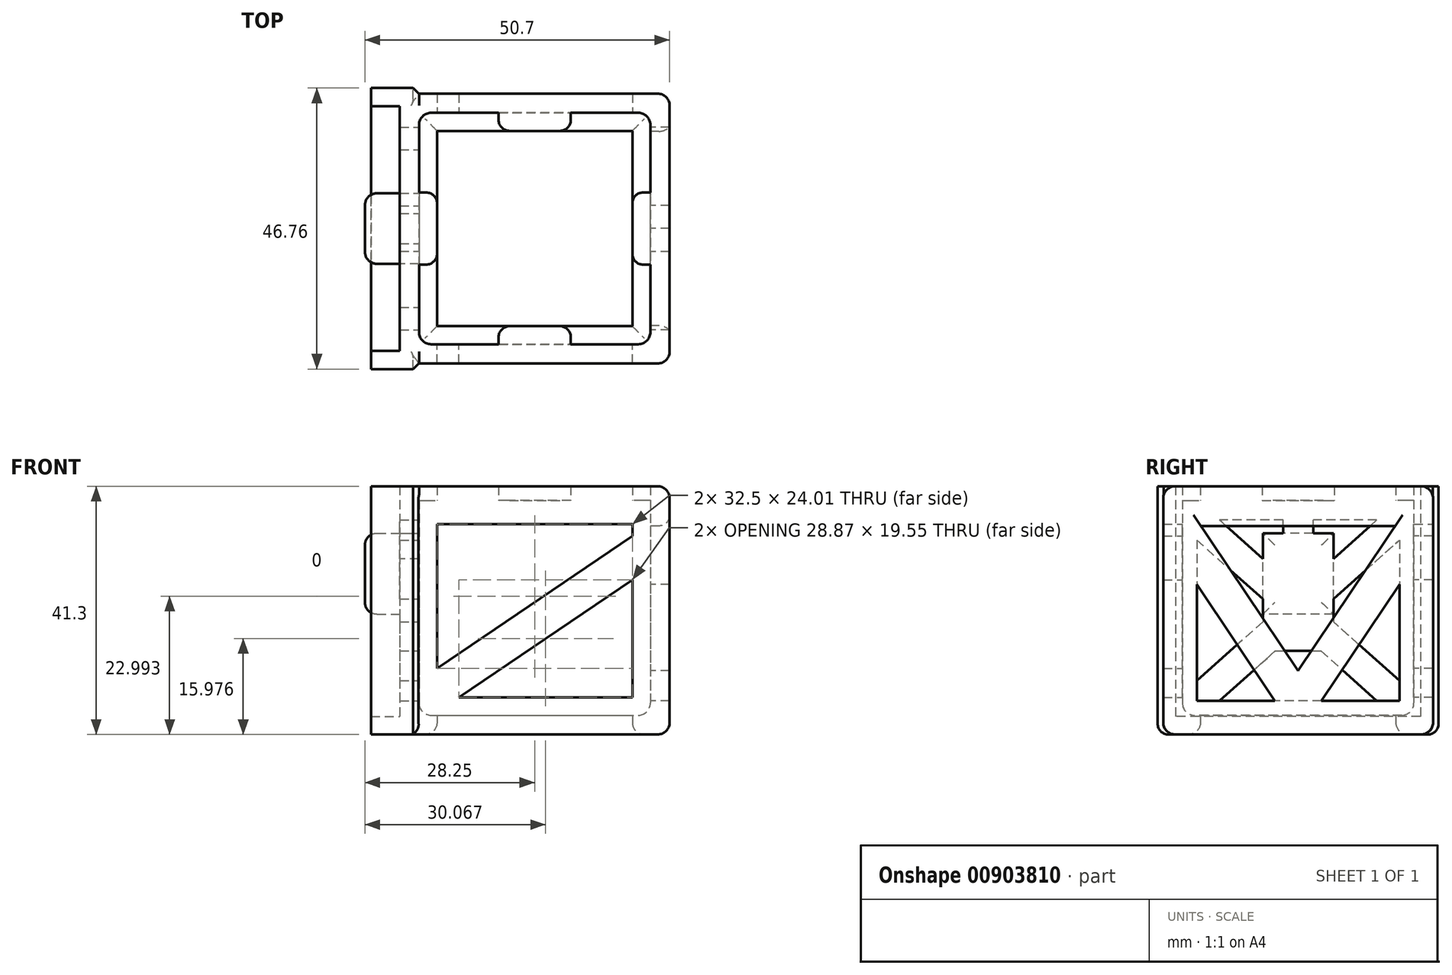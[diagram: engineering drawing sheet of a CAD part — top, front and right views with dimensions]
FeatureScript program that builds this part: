
annotation { "Feature Type Name" : "Feature", "Feature Type Description" : "" }
export const myFeature = defineFeature(function(context is Context, id is Id, definition is map)
    precondition{}
    {
        {
            var Q0;
            Q0=qCreatedBy(makeId("Top.planeOp"),FACE);
            var sketch = newSketch(context, id + "F0", { "sketchPlane" : qUnion([Q0])});
            skLineSegment(sketch, "E0.bottom", {"start": v(-22.45, 22.45) * mm, "end": v(22.45, 22.45) * mm});
            skLineSegment(sketch, "E0.top", {"start": v(-22.45, -22.45) * mm, "end": v(22.45, -22.45) * mm});
            skLineSegment(sketch, "E0.left", {"start": v(-22.45, 22.45) * mm, "end": v(-22.45, -22.45) * mm});
            skLineSegment(sketch, "E0.right", {"start": v(22.45, 22.45) * mm, "end": v(22.45, -22.45) * mm});
            skLineSegment(sketch, "E1.bottom", {"start": v(-19.25, 19.25) * mm, "end": v(19.25, 19.25) * mm});
            skLineSegment(sketch, "E1.top", {"start": v(-19.25, -19.25) * mm, "end": v(19.25, -19.25) * mm});
            skLineSegment(sketch, "E1.left", {"start": v(-19.25, 19.25) * mm, "end": v(-19.25, -19.25) * mm});
            skLineSegment(sketch, "E1.right", {"start": v(19.25, 19.25) * mm, "end": v(19.25, -19.25) * mm});
            skSolve(sketch);
        }
        {
            var Q0;
            Q0 = qSketchRegion(id + "F0", true);
            extrude(context, id + "F1", {"entities" : qUnion([Q0]), "depth" : 41.3 * mm, "offsetDistance" : 25 * mm});
        }
        {
            var Q0;
            Q0=makeQuery(id+"F1.opExtrude","CAP_FACE",FACE,{"disambiguationData":[OSD([sQuery(id+"F0.wireOp",EDGE,"E0.bottom"),sQuery(id+"F0.wireOp",EDGE,"E0.top"),sQuery(id+"F0.wireOp",EDGE,"E0.left"),sQuery(id+"F0.wireOp",EDGE,"E0.right"),sQuery(id+"F0.wireOp",EDGE,"E1.bottom"),sQuery(id+"F0.wireOp",EDGE,"E1.top"),sQuery(id+"F0.wireOp",EDGE,"E1.left"),sQuery(id+"F0.wireOp",EDGE,"E1.right")])],"isStart":false});
            cPlane(context, id + "F2", {"entities" : qUnion([Q0]), "cplaneType" : CPlaneType.OFFSET, "offset" : 2.35 * mm, "oppositeDirection" : true, "width" : 150 * mm, "height" : 150 * mm});
        }
        {
            var Q0;
            Q0=qCreatedBy(id+"F2.planeOp",FACE);
            var sketch = newSketch(context, id + "F3", { "sketchPlane" : qUnion([Q0])});
            skLineSegment(sketch, "E2.bottom", {"start": v(-19.25, 6) * mm, "end": v(-16.25, 6) * mm});
            skLineSegment(sketch, "E2.top", {"start": v(-19.25, -6) * mm, "end": v(-16.25, -6) * mm});
            skLineSegment(sketch, "E2.left", {"start": v(-19.25, 6) * mm, "end": v(-19.25, -6) * mm});
            skLineSegment(sketch, "E2.right", {"start": v(-16.25, 6) * mm, "end": v(-16.25, -6) * mm});
            skLineSegment(sketch, "E3.1.0", {"start": v(-6, -19.25) * mm, "end": v(6, -19.25) * mm});
            skLineSegment(sketch, "E3.1.1", {"start": v(6, -19.25) * mm, "end": v(6, -16.25) * mm});
            skLineSegment(sketch, "E3.1.2", {"start": v(-6, -16.25) * mm, "end": v(6, -16.25) * mm});
            skLineSegment(sketch, "E3.1.3", {"start": v(-6, -19.25) * mm, "end": v(-6, -16.25) * mm});
            skLineSegment(sketch, "E3.2.0", {"start": v(19.25, -6) * mm, "end": v(19.25, 6) * mm});
            skLineSegment(sketch, "E3.2.1", {"start": v(19.25, 6) * mm, "end": v(16.25, 6) * mm});
            skLineSegment(sketch, "E3.2.2", {"start": v(16.25, -6) * mm, "end": v(16.25, 6) * mm});
            skLineSegment(sketch, "E3.2.3", {"start": v(19.25, -6) * mm, "end": v(16.25, -6) * mm});
            skLineSegment(sketch, "E3.3.0", {"start": v(6, 19.25) * mm, "end": v(-6, 19.25) * mm});
            skLineSegment(sketch, "E3.3.1", {"start": v(-6, 19.25) * mm, "end": v(-6, 16.25) * mm});
            skLineSegment(sketch, "E3.3.2", {"start": v(6, 16.25) * mm, "end": v(-6, 16.25) * mm});
            skLineSegment(sketch, "E3.3.3", {"start": v(6, 19.25) * mm, "end": v(6, 16.25) * mm});
            skPoint(sketch, "E3.center", {"position": v(0, 0) * mm});
            skSolve(sketch);
        }
        {
            var Q0;
            Q0 = qSketchRegion(id + "F3", true);
            extrude(context, id + "F4", {"entities" : qUnion([Q0]), "operationType" : NewBodyOperationType.ADD, "depth" : 2.35 * mm, "offsetDistance" : 25 * mm});
        }
        {
            var Q0;
            Q0=qCreatedBy(makeId("Top.planeOp"),FACE);
            var sketch = newSketch(context, id + "F5", { "sketchPlane" : qUnion([Q0])});
            skLineSegment(sketch, "E4.bottom", {"start": v(-16.25, -16.25) * mm, "end": v(16.25, -16.25) * mm});
            skLineSegment(sketch, "E4.top", {"start": v(-16.25, 16.25) * mm, "end": v(16.25, 16.25) * mm});
            skLineSegment(sketch, "E4.left", {"start": v(-16.25, -16.25) * mm, "end": v(-16.25, 16.25) * mm});
            skLineSegment(sketch, "E4.right", {"start": v(16.25, -16.25) * mm, "end": v(16.25, 16.25) * mm});
            skLineSegment(sketch, "E5.bottom", {"start": v(22.45, 22.45) * mm, "end": v(-22.45, 22.45) * mm});
            skLineSegment(sketch, "E5.top", {"start": v(22.45, -22.45) * mm, "end": v(-22.45, -22.45) * mm});
            skLineSegment(sketch, "E5.left", {"start": v(22.45, 22.45) * mm, "end": v(22.45, -22.45) * mm});
            skLineSegment(sketch, "E5.right", {"start": v(-22.45, 22.45) * mm, "end": v(-22.45, -22.45) * mm});
            skSolve(sketch);
        }
        {
            var Q0;
            Q0 = qSketchRegion(id + "F5", true);
            extrude(context, id + "F6", {"entities" : qUnion([Q0]), "operationType" : NewBodyOperationType.ADD, "depth" : 3.2 * mm, "offsetDistance" : 25 * mm});
        }
        {
            var Q0;
            Q0=makeQuery(id+"F1.opExtrude","SWEPT_FACE",FACE,{"disambiguationData":[OSD([sQuery(id+"F0.wireOp",EDGE,"E1.top")])]});
            var sketch = newSketch(context, id + "F7", { "sketchPlane" : qUnion([Q0])});
            skLineSegment(sketch, "E6.bottom", {"start": v(-16.25, 35) * mm, "end": v(16.25, 35) * mm});
            skLineSegment(sketch, "E6.top", {"start": v(-16.25, 6.2) * mm, "end": v(16.25, 6.2) * mm});
            skLineSegment(sketch, "E6.left", {"start": v(16.25, 6.2) * mm, "end": v(16.25, 35) * mm});
            skLineSegment(sketch, "E6.right", {"start": v(-16.25, 6.2) * mm, "end": v(-16.25, 35) * mm});
            skSolve(sketch);
        }
        {
            var Q0;
            Q0=makeQuery(id+"F7.imprint","IMPRINT",FACE,{"disambiguationData":[TD([[makeQuery(id+"F7.imprint","IMPRINT",EDGE,{"derivedFrom":sQuery(id+"F7.wireOp",EDGE,"E6.bottom")}),-1.0]])]});
            extrude(context, id + "F8", {"entities" : qUnion([Q0]), "operationType" : NewBodyOperationType.REMOVE, "endBound" : BoundingType.SYMMETRIC, "oppositeDirection" : true, "depth" : 100 * mm, "offsetDistance" : 25 * mm});
        }
        {
            var Q0;
            Q0=makeQuery(id+"F1.opExtrude","SWEPT_FACE",FACE,{"disambiguationData":[OSD([sQuery(id+"F0.wireOp",EDGE,"E1.left")])]});
            var sketch = newSketch(context, id + "F9", { "sketchPlane" : qUnion([Q0])});
            skLineSegment(sketch, "E7.bottom", {"start": v(-16.85, 35.7) * mm, "end": v(16.85, 35.7) * mm});
            skLineSegment(sketch, "E7.top", {"start": v(-16.85, 5.6) * mm, "end": v(16.85, 5.6) * mm});
            skLineSegment(sketch, "E7.left", {"start": v(16.85, 5.6) * mm, "end": v(16.85, 35.7) * mm});
            skLineSegment(sketch, "E7.right", {"start": v(-16.85, 5.6) * mm, "end": v(-16.85, 35.7) * mm});
            skSolve(sketch);
        }
        {
            var Q0;
            Q0 = qSketchRegion(id + "F9", true);
            extrude(context, id + "F10", {"entities" : qUnion([Q0]), "operationType" : NewBodyOperationType.REMOVE, "endBound" : BoundingType.SYMMETRIC, "depth" : 100 * mm, "offsetDistance" : 25 * mm});
        }
        {
            var Q0;
            Q0=makeQuery(id+"F1.opExtrude","SWEPT_FACE",FACE,{"disambiguationData":[OSD([sQuery(id+"F0.wireOp",EDGE,"E1.left")])]});
            var sketch = newSketch(context, id + "F11", { "sketchPlane" : qUnion([Q0])});
            skLineSegment(sketch, "E8", {"start": v(16.85, 8.95) * mm, "end": v(5.88, 18.75) * mm});
            skLineSegment(sketch, "E9", {"start": v(-16.85, 32.35) * mm, "end": v(-5.88, 22.55) * mm});
            skLineSegment(sketch, "E10", {"start": v(13.1, 35.7) * mm, "end": v(3.8, 27.4) * mm});
            skLineSegment(sketch, "E11", {"start": v(-13.1, 5.6) * mm, "end": v(-3.8, 13.9) * mm});
            skLineSegment(sketch, "E12.trimOffspring", {"start": v(-5.88, 18.75) * mm, "end": v(-16.85, 8.95) * mm});
            skLineSegment(sketch, "E13.trimOffspring", {"start": v(3.8, 13.9) * mm, "end": v(13.1, 5.6) * mm});
            skLineSegment(sketch, "E14.trimOffspring", {"start": v(5.88, 22.55) * mm, "end": v(16.85, 32.35) * mm});
            skLineSegment(sketch, "E15.trimOffspring", {"start": v(-3.8, 27.4) * mm, "end": v(-13.1, 35.7) * mm});
            skLineSegment(sketch, "E16", {"start": v(-16.85, 5.6) * mm, "end": v(16.85, 35.7) * mm, "construction": true});
            skLineSegment(sketch, "E17", {"start": v(-16.85, 35.7) * mm, "end": v(16.85, 5.6) * mm, "construction": true});
            skLineSegment(sketch, "E18.bottom", {"start": v(-3.8, 27.4) * mm, "end": v(-2.5, 27.4) * mm});
            skLineSegment(sketch, "E18.top", {"start": v(-3.8, 13.9) * mm, "end": v(3.8, 13.9) * mm});
            skLineSegment(sketch, "E19.trimOffspring", {"start": v(-5.88, 22.55) * mm, "end": v(-5.88, 18.75) * mm});
            skLineSegment(sketch, "E20.trimOffspring", {"start": v(5.87, 22.55) * mm, "end": v(5.88, 18.75) * mm});
            skLineSegment(sketch, "E21.bottom", {"start": v(-13.1, 35.7) * mm, "end": v(13.1, 35.7) * mm});
            skLineSegment(sketch, "E21.top", {"start": v(-13.1, 5.6) * mm, "end": v(13.1, 5.6) * mm});
            skLineSegment(sketch, "E21.right", {"start": v(16.85, 32.35) * mm, "end": v(16.85, 8.95) * mm});
            skLineSegment(sketch, "E22.trimOffspring", {"start": v(-16.85, 32.35) * mm, "end": v(-16.85, 8.95) * mm});
            skPoint(sketch, "E23", {"position": v(0, 20.65) * mm});
            skLineSegment(sketch, "E24", {"start": v(2.5, 27.4) * mm, "end": v(2.5, 35.7) * mm});
            skLineSegment(sketch, "E25", {"start": v(-2.5, 27.4) * mm, "end": v(-2.5, 35.7) * mm});
            skLineSegment(sketch, "E26.trimOffspring", {"start": v(2.5, 27.4) * mm, "end": v(3.8, 27.4) * mm});
            skSolve(sketch);
        }
        {
            var Q0;
            {var subQ4=sQuery(id+"F11.wireOp",EDGE,"E8");Q0=makeQuery(id+"F11.imprint","IMPRINT",FACE,{"disambiguationData":[TD([[makeQuery(id+"F11.imprint","IMPRINT",EDGE,{"derivedFrom":subQ4}),1.0]])]});}
            extrude(context, id + "F12", {"entities" : qUnion([Q0]), "operationType" : NewBodyOperationType.ADD, "oppositeDirection" : true, "depth" : 3.2 * mm, "offsetDistance" : 25 * mm});
        }
        {
            var Q0;
            Q0=makeQuery(id+"F11.imprint","IMPRINT",FACE,{"disambiguationData":[TD([[makeQuery(id+"F11.imprint","IMPRINT",EDGE,{"derivedFrom":sQuery(id+"F11.wireOp",EDGE,"E9")}),-1.0]])]});
            var sketch = newSketch(context, id + "F13", { "sketchPlane" : qUnion([Q0])});
            skLineSegment(sketch, "E27", {"start": v(-23.38, 0) * mm, "end": v(-23.38, 41.3) * mm});
            skLineSegment(sketch, "E28", {"start": v(-23.38, 41.3) * mm, "end": v(-20.38, 41.3) * mm});
            skLineSegment(sketch, "E29", {"start": v(23.37, 41.3) * mm, "end": v(23.38, 0) * mm});
            skLineSegment(sketch, "E30", {"start": v(-23.38, 0) * mm, "end": v(23.37, 0) * mm});
            skLineSegment(sketch, "E31.left", {"start": v(-20.38, 41.3) * mm, "end": v(-20.38, 3) * mm});
            skLineSegment(sketch, "E31.right", {"start": v(20.37, 41.3) * mm, "end": v(20.38, 3) * mm});
            skLineSegment(sketch, "E32.trimOffspring", {"start": v(20.37, 41.3) * mm, "end": v(23.37, 41.3) * mm});
            skLineSegment(sketch, "E33", {"start": v(20.38, 3) * mm, "end": v(-20.38, 3) * mm});
            skSolve(sketch);
        }
        {
            var Q0;
            Q0 = qSketchRegion(id + "F13", true);
            extrude(context, id + "F14", {"entities" : qUnion([Q0]), "operationType" : NewBodyOperationType.ADD, "oppositeDirection" : true, "depth" : 8 * mm, "offsetDistance" : 25 * mm, "hasSecondDirection" : true, "secondDirectionOppositeDirection" : false, "secondDirectionDepth" : 0 * mm});
        }
        {
            var Q0;
            Q0=makeQuery(id+"F1.opExtrude","SWEPT_FACE",FACE,{"disambiguationData":[OSD([sQuery(id+"F0.wireOp",EDGE,"E1.right")])]});
            var sketch = newSketch(context, id + "F15", { "sketchPlane" : qUnion([Q0])});
            skLineSegment(sketch, "E34", {"start": v(-3.87, 5.6) * mm, "end": v(-16.85, 24.94) * mm});
            skLineSegment(sketch, "E35", {"start": v(16.18, 34.7) * mm, "end": v(0, 10.6) * mm});
            skLineSegment(sketch, "E36", {"start": v(16.85, 24.94) * mm, "end": v(3.87, 5.6) * mm});
            skLineSegment(sketch, "E37", {"start": v(0, 10.6) * mm, "end": v(-16.18, 34.7) * mm});
            skLineSegment(sketch, "E38", {"start": v(16.85, 24.94) * mm, "end": v(16.85, 35.7) * mm});
            skLineSegment(sketch, "E39", {"start": v(16.18, 34.7) * mm, "end": v(-16.18, 34.7) * mm});
            skSolve(sketch);
        }
        {
            var Q0;
            Q0=makeQuery(id+"F15.imprint","IMPRINT",FACE,{"disambiguationData":[TD([[makeQuery(id+"F15.imprint","IMPRINT",EDGE,{"derivedFrom":sQuery(id+"F15.wireOp",EDGE,"E34")}),-1.0]])]});
            extrude(context, id + "F16", {"entities" : qUnion([Q0]), "operationType" : NewBodyOperationType.ADD, "oppositeDirection" : true, "depth" : 3.2 * mm, "offsetDistance" : 25 * mm});
        }
        {
            var Q0;
            {var subQ0=sQuery(id+"F11.wireOp",EDGE,"E8");var subQ1=sQuery(id+"F0.wireOp",EDGE,"E1.left");Q0=makeQuery(id+"F12.boolean.opBoolean","MERGE",FACE,{"derivedFrom":[makeQuery(id+"F1.opExtrude","SWEPT_FACE",FACE,{"disambiguationData":[OSD([subQ1])]}),makeQuery(id+"F12.opExtrude","CAP_FACE",FACE,{"disambiguationData":[OSD([sQuery(id+"F0.wireOp",EDGE,"E1.top"),subQ1,sQuery(id+"F11.wireOp",EDGE,"8725238e-58d9-4992-a780-614409748a7c.top"),sQuery(id+"F11.wireOp",EDGE,"8725238e-58d9-4992-a780-614409748a7c.right"),subQ0])],"isStart":true}),makeQuery(id+"F12.opExtrude","CAP_FACE",FACE,{"disambiguationData":[OSD([subQ1,sQuery(id+"F9.wireOp",EDGE,"E7.bottom"),sQuery(id+"F9.wireOp",EDGE,"E7.top"),sQuery(id+"F9.wireOp",EDGE,"E7.left"),sQuery(id+"F9.wireOp",EDGE,"E7.right"),subQ0,sQuery(id+"F11.wireOp",EDGE,"E9"),sQuery(id+"F11.wireOp",EDGE,"E10"),sQuery(id+"F11.wireOp",EDGE,"E11"),sQuery(id+"F11.wireOp",EDGE,"E12.trimOffspring"),sQuery(id+"F11.wireOp",EDGE,"E13.trimOffspring"),sQuery(id+"F11.wireOp",EDGE,"E14.trimOffspring"),sQuery(id+"F11.wireOp",EDGE,"E15.trimOffspring"),sQuery(id+"F11.wireOp",EDGE,"E18.bottom"),sQuery(id+"F11.wireOp",EDGE,"E18.top"),sQuery(id+"F11.wireOp",EDGE,"E19.trimOffspring"),sQuery(id+"F11.wireOp",EDGE,"E20.trimOffspring")])],"isStart":true})]});}
            var sketch = newSketch(context, id + "F17", { "sketchPlane" : qUnion([Q0])});
            skLineSegment(sketch, "E40.bottom", {"start": v(5.87, 20) * mm, "end": v(-5.88, 20) * mm});
            skLineSegment(sketch, "E40.top", {"start": v(5.87, 33.5) * mm, "end": v(-5.88, 33.5) * mm});
            skLineSegment(sketch, "E40.left", {"start": v(5.87, 20) * mm, "end": v(5.87, 33.5) * mm});
            skLineSegment(sketch, "E40.right", {"start": v(-5.88, 20) * mm, "end": v(-5.88, 33.5) * mm});
            skSolve(sketch);
        }
        {
            var Q0;
            Q0 = qSketchRegion(id + "F17", true);
            extrude(context, id + "F18", {"entities" : qUnion([Q0]), "operationType" : NewBodyOperationType.ADD, "oppositeDirection" : true, "depth" : 9 * mm, "offsetDistance" : 25 * mm});
        }
        {
            var Q0;
            Q0=makeQuery(id+"F1.opExtrude","SWEPT_FACE",FACE,{"disambiguationData":[OSD([sQuery(id+"F0.wireOp",EDGE,"E1.bottom")])]});
            var sketch = newSketch(context, id + "F19", { "sketchPlane" : qUnion([Q0])});
            skLineSegment(sketch, "E41", {"start": v(16.25, 25.75) * mm, "end": v(-12.62, 6.2) * mm});
            skLineSegment(sketch, "E42", {"start": v(-16.25, 10.99) * mm, "end": v(16.25, 33) * mm});
            skSolve(sketch);
        }
        {
            var Q0;
            {var subQ5=sQuery(id+"F19.wireOp",EDGE,"E41");Q0=makeQuery(id+"F19.imprint","IMPRINT",FACE,{"disambiguationData":[TD([[makeQuery(id+"F19.imprint","IMPRINT",EDGE,{"derivedFrom":subQ5}),-1.0]])]});}
            extrude(context, id + "F20", {"entities" : qUnion([Q0]), "operationType" : NewBodyOperationType.ADD, "oppositeDirection" : true, "depth" : 3.2 * mm, "offsetDistance" : 25 * mm});
        }
        {
            var Q0;
            Q0=makeQuery(id+"F1.opExtrude","SWEPT_FACE",FACE,{"disambiguationData":[OSD([sQuery(id+"F0.wireOp",EDGE,"E1.top")])]});
            var sketch = newSketch(context, id + "F21", { "sketchPlane" : qUnion([Q0])});
            skLineSegment(sketch, "E43.0", {"start": v(-16.25, 25.75) * mm, "end": v(12.62, 6.2) * mm});
            skLineSegment(sketch, "E43.1", {"start": v(16.25, 10.99) * mm, "end": v(-16.25, 33) * mm});
            skSolve(sketch);
        }
        {
            var Q0;
            Q0=makeQuery(id+"F1.opExtrude","CAP_EDGE",EDGE,{"disambiguationData":[OSD([sQuery(id+"F0.wireOp",EDGE,"E0.bottom")])],"isStart":true});
            var Q1;
            Q1=makeQuery(id+"F1.opExtrude","SWEPT_EDGE",EDGE,{"disambiguationData":[OSD([sQuery(id+"F0.wireOp",EDGE,"E0.bottom"),sQuery(id+"F0.wireOp",EDGE,"E0.right")])]});
            var Q2;
            Q2=makeQuery(id+"F1.opExtrude","CAP_EDGE",EDGE,{"disambiguationData":[OSD([sQuery(id+"F0.wireOp",EDGE,"E0.bottom")])],"isStart":false});
            var Q3;
            Q3=makeQuery(id+"F6.boolean.opBoolean","INTERSECT",EDGE,{"derivedFrom":[makeQuery(id+"F1.opExtrude","SWEPT_FACE",FACE,{"disambiguationData":[OSD([sQuery(id+"F0.wireOp",EDGE,"E1.bottom")])]}),makeQuery(id+"F6.opExtrude","CAP_FACE",FACE,{"disambiguationData":[OSD([sQuery(id+"F5.wireOp",EDGE,"E4.bottom"),sQuery(id+"F5.wireOp",EDGE,"E4.top"),sQuery(id+"F5.wireOp",EDGE,"E4.left"),sQuery(id+"F5.wireOp",EDGE,"E4.right"),sQuery(id+"F5.wireOp",EDGE,"E5.bottom"),sQuery(id+"F5.wireOp",EDGE,"E5.top"),sQuery(id+"F5.wireOp",EDGE,"E5.left"),sQuery(id+"F5.wireOp",EDGE,"E5.right")])],"isStart":false})]});
            var Q4;
            Q4=makeQuery(id+"F6.boolean.opBoolean","INTERSECT",EDGE,{"derivedFrom":[makeQuery(id+"F1.opExtrude","SWEPT_FACE",FACE,{"disambiguationData":[OSD([sQuery(id+"F0.wireOp",EDGE,"E1.top")])]}),makeQuery(id+"F6.opExtrude","CAP_FACE",FACE,{"disambiguationData":[OSD([sQuery(id+"F5.wireOp",EDGE,"E4.bottom"),sQuery(id+"F5.wireOp",EDGE,"E4.top"),sQuery(id+"F5.wireOp",EDGE,"E4.left"),sQuery(id+"F5.wireOp",EDGE,"E4.right"),sQuery(id+"F5.wireOp",EDGE,"E5.bottom"),sQuery(id+"F5.wireOp",EDGE,"E5.top"),sQuery(id+"F5.wireOp",EDGE,"E5.left"),sQuery(id+"F5.wireOp",EDGE,"E5.right")])],"isStart":false})]});
            var Q5;
            Q5=makeQuery(id+"F1.opExtrude","CAP_EDGE",EDGE,{"disambiguationData":[OSD([sQuery(id+"F0.wireOp",EDGE,"E0.top")])],"isStart":true});
            var Q6;
            Q6=makeQuery(id+"F1.opExtrude","CAP_EDGE",EDGE,{"disambiguationData":[OSD([sQuery(id+"F0.wireOp",EDGE,"E0.right")])],"isStart":true});
            var Q7;
            Q7=makeQuery(id+"F1.opExtrude","SWEPT_EDGE",EDGE,{"disambiguationData":[OSD([sQuery(id+"F0.wireOp",EDGE,"E0.top"),sQuery(id+"F0.wireOp",EDGE,"E0.right")])]});
            var Q8;
            Q8=makeQuery(id+"F6.opExtrude","CAP_EDGE",EDGE,{"disambiguationData":[OSD([sQuery(id+"F5.wireOp",EDGE,"E4.left")])],"isStart":true});
            var Q9;
            Q9=makeQuery(id+"F6.opExtrude","CAP_EDGE",EDGE,{"disambiguationData":[OSD([sQuery(id+"F5.wireOp",EDGE,"E4.bottom")])],"isStart":true});
            var Q10;
            Q10=makeQuery(id+"F6.opExtrude","CAP_EDGE",EDGE,{"disambiguationData":[OSD([sQuery(id+"F5.wireOp",EDGE,"E4.right")])],"isStart":true});
            var Q11;
            Q11=makeQuery(id+"F6.opExtrude","CAP_EDGE",EDGE,{"disambiguationData":[OSD([sQuery(id+"F5.wireOp",EDGE,"E4.top")])],"isStart":true});
            var Q12;
            Q12=makeQuery(id+"F1.opExtrude","CAP_EDGE",EDGE,{"disambiguationData":[OSD([sQuery(id+"F0.wireOp",EDGE,"E0.top")])],"isStart":false});
            var Q13;
            Q13=makeQuery(id+"F1.opExtrude","CAP_EDGE",EDGE,{"disambiguationData":[OSD([sQuery(id+"F0.wireOp",EDGE,"E0.right")])],"isStart":false});
            var Q14;
            Q14=makeQuery(id+"F4.opExtrude","SWEPT_EDGE",EDGE,{"disambiguationData":[OSD([sQuery(id+"F3.wireOp",EDGE,"E3.3.0"),sQuery(id+"F3.wireOp",EDGE,"E3.3.3")])]});
            var Q15;
            Q15=makeQuery(id+"F4.opExtrude","SWEPT_EDGE",EDGE,{"disambiguationData":[OSD([sQuery(id+"F3.wireOp",EDGE,"E3.3.0"),sQuery(id+"F3.wireOp",EDGE,"E3.3.1")])]});
            var Q16;
            Q16=makeQuery(id+"F4.opExtrude","SWEPT_EDGE",EDGE,{"disambiguationData":[OSD([sQuery(id+"F3.wireOp",EDGE,"E3.2.0"),sQuery(id+"F3.wireOp",EDGE,"E3.2.3")])]});
            var Q17;
            Q17=makeQuery(id+"F4.opExtrude","SWEPT_EDGE",EDGE,{"disambiguationData":[OSD([sQuery(id+"F3.wireOp",EDGE,"E3.2.0"),sQuery(id+"F3.wireOp",EDGE,"E3.2.1")])]});
            var Q18;
            Q18=makeQuery(id+"F4.opExtrude","SWEPT_EDGE",EDGE,{"disambiguationData":[OSD([sQuery(id+"F3.wireOp",EDGE,"E3.1.0"),sQuery(id+"F3.wireOp",EDGE,"E3.1.3")])]});
            var Q19;
            Q19=makeQuery(id+"F4.opExtrude","SWEPT_EDGE",EDGE,{"disambiguationData":[OSD([sQuery(id+"F3.wireOp",EDGE,"E3.1.0"),sQuery(id+"F3.wireOp",EDGE,"E3.1.1")])]});
            var Q20;
            Q20=makeQuery(id+"F4.opExtrude","SWEPT_EDGE",EDGE,{"disambiguationData":[OSD([sQuery(id+"F3.wireOp",EDGE,"E2.bottom"),sQuery(id+"F3.wireOp",EDGE,"E2.left")])]});
            var Q21;
            Q21=makeQuery(id+"F4.opExtrude","SWEPT_EDGE",EDGE,{"disambiguationData":[OSD([sQuery(id+"F3.wireOp",EDGE,"E2.top"),sQuery(id+"F3.wireOp",EDGE,"E2.left")])]});
            var Q22;
            Q22=makeQuery(id+"F1.opExtrude","SWEPT_EDGE",EDGE,{"disambiguationData":[OSD([sQuery(id+"F0.wireOp",EDGE,"E1.top"),sQuery(id+"F0.wireOp",EDGE,"E1.left")])]});
            var Q23;
            Q23=makeQuery(id+"F1.opExtrude","SWEPT_EDGE",EDGE,{"disambiguationData":[OSD([sQuery(id+"F0.wireOp",EDGE,"E1.bottom"),sQuery(id+"F0.wireOp",EDGE,"E1.left")])]});
            var Q24;
            Q24=makeQuery(id+"F6.boolean.opBoolean","INTERSECT",EDGE,{"derivedFrom":[makeQuery(id+"F1.opExtrude","SWEPT_FACE",FACE,{"disambiguationData":[OSD([sQuery(id+"F0.wireOp",EDGE,"E1.right")])]}),makeQuery(id+"F6.opExtrude","CAP_FACE",FACE,{"disambiguationData":[OSD([sQuery(id+"F5.wireOp",EDGE,"E4.bottom"),sQuery(id+"F5.wireOp",EDGE,"E4.top"),sQuery(id+"F5.wireOp",EDGE,"E4.left"),sQuery(id+"F5.wireOp",EDGE,"E4.right"),sQuery(id+"F5.wireOp",EDGE,"E5.bottom"),sQuery(id+"F5.wireOp",EDGE,"E5.top"),sQuery(id+"F5.wireOp",EDGE,"E5.left"),sQuery(id+"F5.wireOp",EDGE,"E5.right")])],"isStart":false})]});
            var Q25;
            Q25=makeQuery(id+"F1.opExtrude","SWEPT_EDGE",EDGE,{"disambiguationData":[OSD([sQuery(id+"F0.wireOp",EDGE,"E1.top"),sQuery(id+"F0.wireOp",EDGE,"E1.right")])]});
            var Q26;
            Q26=makeQuery(id+"F1.opExtrude","SWEPT_EDGE",EDGE,{"disambiguationData":[OSD([sQuery(id+"F0.wireOp",EDGE,"E1.bottom"),sQuery(id+"F0.wireOp",EDGE,"E1.right")])]});
            var Q27;
            Q27=makeQuery(id+"F18.opExtrude","CAP_EDGE",EDGE,{"disambiguationData":[OSD([sQuery(id+"F17.wireOp",EDGE,"E40.top")])],"isStart":false});
            var Q28;
            Q28=makeQuery(id+"F18.opExtrude","CAP_EDGE",EDGE,{"disambiguationData":[OSD([sQuery(id+"F17.wireOp",EDGE,"E40.right")])],"isStart":false});
            var Q29;
            Q29=makeQuery(id+"F18.opExtrude","CAP_EDGE",EDGE,{"disambiguationData":[OSD([sQuery(id+"F17.wireOp",EDGE,"E40.bottom")])],"isStart":false});
            var Q30;
            Q30=makeQuery(id+"F18.opExtrude","CAP_EDGE",EDGE,{"disambiguationData":[OSD([sQuery(id+"F17.wireOp",EDGE,"E40.left")])],"isStart":false});
            var Q31;
            Q31=makeQuery(id+"F6.boolean.opBoolean","INTERSECT",EDGE,{"derivedFrom":[makeQuery(id+"F1.opExtrude","SWEPT_FACE",FACE,{"disambiguationData":[OSD([sQuery(id+"F0.wireOp",EDGE,"E1.left")])]}),makeQuery(id+"F6.opExtrude","CAP_FACE",FACE,{"disambiguationData":[OSD([sQuery(id+"F5.wireOp",EDGE,"E4.bottom"),sQuery(id+"F5.wireOp",EDGE,"E4.top"),sQuery(id+"F5.wireOp",EDGE,"E4.left"),sQuery(id+"F5.wireOp",EDGE,"E4.right"),sQuery(id+"F5.wireOp",EDGE,"E5.bottom"),sQuery(id+"F5.wireOp",EDGE,"E5.top"),sQuery(id+"F5.wireOp",EDGE,"E5.left"),sQuery(id+"F5.wireOp",EDGE,"E5.right")])],"isStart":false})]});
            fillet(context, id + "F22", {"entities" : qUnion([Q0, Q1, Q2, Q3, Q4, Q5, Q6, Q7, Q8, Q9, Q10, Q11, Q12, Q13, Q14, Q15, Q16, Q17, Q18, Q19, Q20, Q21, Q22, Q23, Q24, Q25, Q26, Q27, Q28, Q29, Q30, Q31]), "radius" : 2 * mm, "allowEdgeOverflow" : false});
        }
        {
            var Q0;
            Q0=makeQuery(id+"F4.opExtrude","SWEPT_EDGE",EDGE,{"disambiguationData":[OSD([sQuery(id+"F3.wireOp",EDGE,"E2.bottom"),sQuery(id+"F3.wireOp",EDGE,"E2.right")])]});
            var Q1;
            Q1=makeQuery(id+"F4.opExtrude","SWEPT_EDGE",EDGE,{"disambiguationData":[OSD([sQuery(id+"F3.wireOp",EDGE,"E2.top"),sQuery(id+"F3.wireOp",EDGE,"E2.right")])]});
            var Q2;
            Q2=makeQuery(id+"F4.opExtrude","SWEPT_EDGE",EDGE,{"disambiguationData":[OSD([sQuery(id+"F3.wireOp",EDGE,"E3.1.2"),sQuery(id+"F3.wireOp",EDGE,"E3.1.3")])]});
            var Q3;
            Q3=makeQuery(id+"F4.opExtrude","SWEPT_EDGE",EDGE,{"disambiguationData":[OSD([sQuery(id+"F3.wireOp",EDGE,"E3.1.1"),sQuery(id+"F3.wireOp",EDGE,"E3.1.2")])]});
            var Q4;
            Q4=makeQuery(id+"F4.opExtrude","SWEPT_EDGE",EDGE,{"disambiguationData":[OSD([sQuery(id+"F3.wireOp",EDGE,"E3.3.2"),sQuery(id+"F3.wireOp",EDGE,"E3.3.3")])]});
            var Q5;
            Q5=makeQuery(id+"F4.opExtrude","SWEPT_EDGE",EDGE,{"disambiguationData":[OSD([sQuery(id+"F3.wireOp",EDGE,"E3.2.2"),sQuery(id+"F3.wireOp",EDGE,"E3.2.3")])]});
            var Q6;
            Q6=makeQuery(id+"F4.opExtrude","SWEPT_EDGE",EDGE,{"disambiguationData":[OSD([sQuery(id+"F3.wireOp",EDGE,"E3.2.1"),sQuery(id+"F3.wireOp",EDGE,"E3.2.2")])]});
            var Q7;
            Q7=makeQuery(id+"F4.opExtrude","SWEPT_EDGE",EDGE,{"disambiguationData":[OSD([sQuery(id+"F3.wireOp",EDGE,"E3.3.1"),sQuery(id+"F3.wireOp",EDGE,"E3.3.2")])]});
            var Q8;
            Q8=makeQuery(id+"F14.opExtrude","SWEPT_EDGE",EDGE,{"disambiguationData":[OSD([sQuery(id+"F13.wireOp",EDGE,"E27"),sQuery(id+"F13.wireOp",EDGE,"E30")])]});
            var Q9;
            Q9=makeQuery(id+"F14.opExtrude","SWEPT_EDGE",EDGE,{"disambiguationData":[OSD([sQuery(id+"F13.wireOp",EDGE,"E29"),sQuery(id+"F13.wireOp",EDGE,"E30")])]});
            var Q10;
            Q10=makeQuery(id+"F16.opExtrude","CAP_EDGE",EDGE,{"disambiguationData":[OSD([sQuery(id+"F15.wireOp",EDGE,"E39")])],"isStart":false});
            fillet(context, id + "F23", {"entities" : qUnion([Q0, Q1, Q2, Q3, Q4, Q5, Q6, Q7, Q8, Q9, Q10]), "radius" : 1.8 * mm, "tangentPropagation" : true, "allowEdgeOverflow" : false});
        }
        {
            var Q0;
            Q0=makeQuery(id+"F14.opExtrude","CAP_EDGE",EDGE,{"disambiguationData":[OSD([sQuery(id+"F13.wireOp",EDGE,"E27")])],"isStart":true});
            var Q1;
            {var subQ0=sQuery(id+"F13.wireOp",EDGE,"E28");var subQ1=sQuery(id+"F13.wireOp",EDGE,"E27");var subQ8=sQuery(id+"F0.wireOp",EDGE,"E0.top");var subQ10=sQuery(id+"F13.wireOp",EDGE,"E32.trimOffspring");var subQ11=sQuery(id+"F13.wireOp",EDGE,"E30");Q1=makeQuery(id+"F23.opFillet","BLEND_EDGE",EDGE,{"blendedFrom":[makeQuery(id+"F14.opExtrude","SWEPT_EDGE",EDGE,{"disambiguationData":[OSD([subQ1,subQ0])]}),makeQuery(id+"F14.boolean.opBoolean","SPLIT",FACE,{"disambiguationData":[TD([makeQuery(id+"F1.opExtrude","SWEPT_FACE",FACE,{"disambiguationData":[OSD([subQ8])]})])],"derivedFrom":makeQuery(id+"F14.opExtrude","CAP_FACE",FACE,{"disambiguationData":[OSD([subQ1,subQ0,sQuery(id+"F13.wireOp",EDGE,"E29"),subQ11,sQuery(id+"F13.wireOp",EDGE,"E31.left"),sQuery(id+"F13.wireOp",EDGE,"E31.right"),subQ10,sQuery(id+"F13.wireOp",EDGE,"E33")])],"isStart":true})})],"blendedInto":[makeQuery(id+"F14.boolean.opBoolean","SPLIT",FACE,{"disambiguationData":[TD([makeQuery(id+"F1.opExtrude","SWEPT_FACE",FACE,{"disambiguationData":[OSD([subQ8])]})])],"derivedFrom":makeQuery(id+"F14.opExtrude","CAP_FACE",FACE,{"disambiguationData":[OSD([subQ1,subQ0,sQuery(id+"F13.wireOp",EDGE,"E29"),subQ11,sQuery(id+"F13.wireOp",EDGE,"E31.left"),sQuery(id+"F13.wireOp",EDGE,"E31.right"),subQ10,sQuery(id+"F13.wireOp",EDGE,"E33")])],"isStart":true})})]});}
            var Q2;
            {var subQ0=sQuery(id+"F13.wireOp",EDGE,"E28");var subQ1=sQuery(id+"F13.wireOp",EDGE,"E27");var subQ8=sQuery(id+"F0.wireOp",EDGE,"E0.top");var subQ10=sQuery(id+"F13.wireOp",EDGE,"E32.trimOffspring");var subQ11=sQuery(id+"F13.wireOp",EDGE,"E30");Q2=makeQuery(id+"F23.opFillet","BLEND_EDGE",EDGE,{"blendedFrom":[makeQuery(id+"F14.opExtrude","SWEPT_EDGE",EDGE,{"disambiguationData":[OSD([subQ1,subQ11])]}),makeQuery(id+"F14.boolean.opBoolean","SPLIT",FACE,{"disambiguationData":[TD([makeQuery(id+"F1.opExtrude","SWEPT_FACE",FACE,{"disambiguationData":[OSD([subQ8])]})])],"derivedFrom":makeQuery(id+"F14.opExtrude","CAP_FACE",FACE,{"disambiguationData":[OSD([subQ1,subQ0,sQuery(id+"F13.wireOp",EDGE,"E29"),subQ11,sQuery(id+"F13.wireOp",EDGE,"E31.left"),sQuery(id+"F13.wireOp",EDGE,"E31.right"),subQ10,sQuery(id+"F13.wireOp",EDGE,"E33")])],"isStart":true})})],"blendedInto":[makeQuery(id+"F14.boolean.opBoolean","SPLIT",FACE,{"disambiguationData":[TD([makeQuery(id+"F1.opExtrude","SWEPT_FACE",FACE,{"disambiguationData":[OSD([subQ8])]})])],"derivedFrom":makeQuery(id+"F14.opExtrude","CAP_FACE",FACE,{"disambiguationData":[OSD([subQ1,subQ0,sQuery(id+"F13.wireOp",EDGE,"E29"),subQ11,sQuery(id+"F13.wireOp",EDGE,"E31.left"),sQuery(id+"F13.wireOp",EDGE,"E31.right"),subQ10,sQuery(id+"F13.wireOp",EDGE,"E33")])],"isStart":true})})]});}
            var Q3;
            {var subQ0=sQuery(id+"F13.wireOp",EDGE,"E29");var subQ1=sQuery(id+"F13.wireOp",EDGE,"E28");var subQ2=sQuery(id+"F0.wireOp",EDGE,"E0.bottom");var subQ3=sQuery(id+"F13.wireOp",EDGE,"E30");var subQ11=sQuery(id+"F13.wireOp",EDGE,"E32.trimOffspring");Q3=makeQuery(id+"F23.opFillet","BLEND_EDGE",EDGE,{"blendedFrom":[makeQuery(id+"F14.opExtrude","SWEPT_EDGE",EDGE,{"disambiguationData":[OSD([subQ0,subQ3])]}),makeQuery(id+"F14.boolean.opBoolean","SPLIT",FACE,{"disambiguationData":[TD([makeQuery(id+"F1.opExtrude","SWEPT_FACE",FACE,{"disambiguationData":[OSD([subQ2])]})])],"derivedFrom":makeQuery(id+"F14.opExtrude","CAP_FACE",FACE,{"disambiguationData":[OSD([sQuery(id+"F13.wireOp",EDGE,"E27"),subQ1,subQ0,subQ3,sQuery(id+"F13.wireOp",EDGE,"E31.left"),sQuery(id+"F13.wireOp",EDGE,"E31.right"),subQ11,sQuery(id+"F13.wireOp",EDGE,"E33")])],"isStart":true})})],"blendedInto":[makeQuery(id+"F14.boolean.opBoolean","SPLIT",FACE,{"disambiguationData":[TD([makeQuery(id+"F1.opExtrude","SWEPT_FACE",FACE,{"disambiguationData":[OSD([subQ2])]})])],"derivedFrom":makeQuery(id+"F14.opExtrude","CAP_FACE",FACE,{"disambiguationData":[OSD([sQuery(id+"F13.wireOp",EDGE,"E27"),subQ1,subQ0,subQ3,sQuery(id+"F13.wireOp",EDGE,"E31.left"),sQuery(id+"F13.wireOp",EDGE,"E31.right"),subQ11,sQuery(id+"F13.wireOp",EDGE,"E33")])],"isStart":true})})]});}
            var Q4;
            Q4=makeQuery(id+"F14.opExtrude","CAP_EDGE",EDGE,{"disambiguationData":[OSD([sQuery(id+"F13.wireOp",EDGE,"E29")])],"isStart":true});
            var Q5;
            {var subQ0=sQuery(id+"F13.wireOp",EDGE,"E29");var subQ1=sQuery(id+"F13.wireOp",EDGE,"E28");var subQ2=sQuery(id+"F0.wireOp",EDGE,"E0.bottom");var subQ3=sQuery(id+"F13.wireOp",EDGE,"E30");var subQ11=sQuery(id+"F13.wireOp",EDGE,"E32.trimOffspring");Q5=makeQuery(id+"F23.opFillet","BLEND_EDGE",EDGE,{"blendedFrom":[makeQuery(id+"F14.opExtrude","SWEPT_EDGE",EDGE,{"disambiguationData":[OSD([subQ0,subQ11])]}),makeQuery(id+"F14.boolean.opBoolean","SPLIT",FACE,{"disambiguationData":[TD([makeQuery(id+"F1.opExtrude","SWEPT_FACE",FACE,{"disambiguationData":[OSD([subQ2])]})])],"derivedFrom":makeQuery(id+"F14.opExtrude","CAP_FACE",FACE,{"disambiguationData":[OSD([sQuery(id+"F13.wireOp",EDGE,"E27"),subQ1,subQ0,subQ3,sQuery(id+"F13.wireOp",EDGE,"E31.left"),sQuery(id+"F13.wireOp",EDGE,"E31.right"),subQ11,sQuery(id+"F13.wireOp",EDGE,"E33")])],"isStart":true})})],"blendedInto":[makeQuery(id+"F14.boolean.opBoolean","SPLIT",FACE,{"disambiguationData":[TD([makeQuery(id+"F1.opExtrude","SWEPT_FACE",FACE,{"disambiguationData":[OSD([subQ2])]})])],"derivedFrom":makeQuery(id+"F14.opExtrude","CAP_FACE",FACE,{"disambiguationData":[OSD([sQuery(id+"F13.wireOp",EDGE,"E27"),subQ1,subQ0,subQ3,sQuery(id+"F13.wireOp",EDGE,"E31.left"),sQuery(id+"F13.wireOp",EDGE,"E31.right"),subQ11,sQuery(id+"F13.wireOp",EDGE,"E33")])],"isStart":true})})]});}
            chamfer(context, id + "F24", {"entities" : qUnion([Q0, Q1, Q2, Q3, Q4, Q5]), "width" : 1 * mm});
        }
        {
            var Q0;
            {var subQ5=sQuery(id+"F21.wireOp",EDGE,"E43.0");Q0=makeQuery(id+"F21.imprint","IMPRINT",FACE,{"disambiguationData":[TD([[makeQuery(id+"F21.imprint","IMPRINT",EDGE,{"derivedFrom":subQ5}),1.0]])]});}
            extrude(context, id + "F25", {"entities" : qUnion([Q0]), "operationType" : NewBodyOperationType.ADD, "oppositeDirection" : true, "depth" : 3.2 * mm, "offsetDistance" : 25 * mm});
        }
    });
